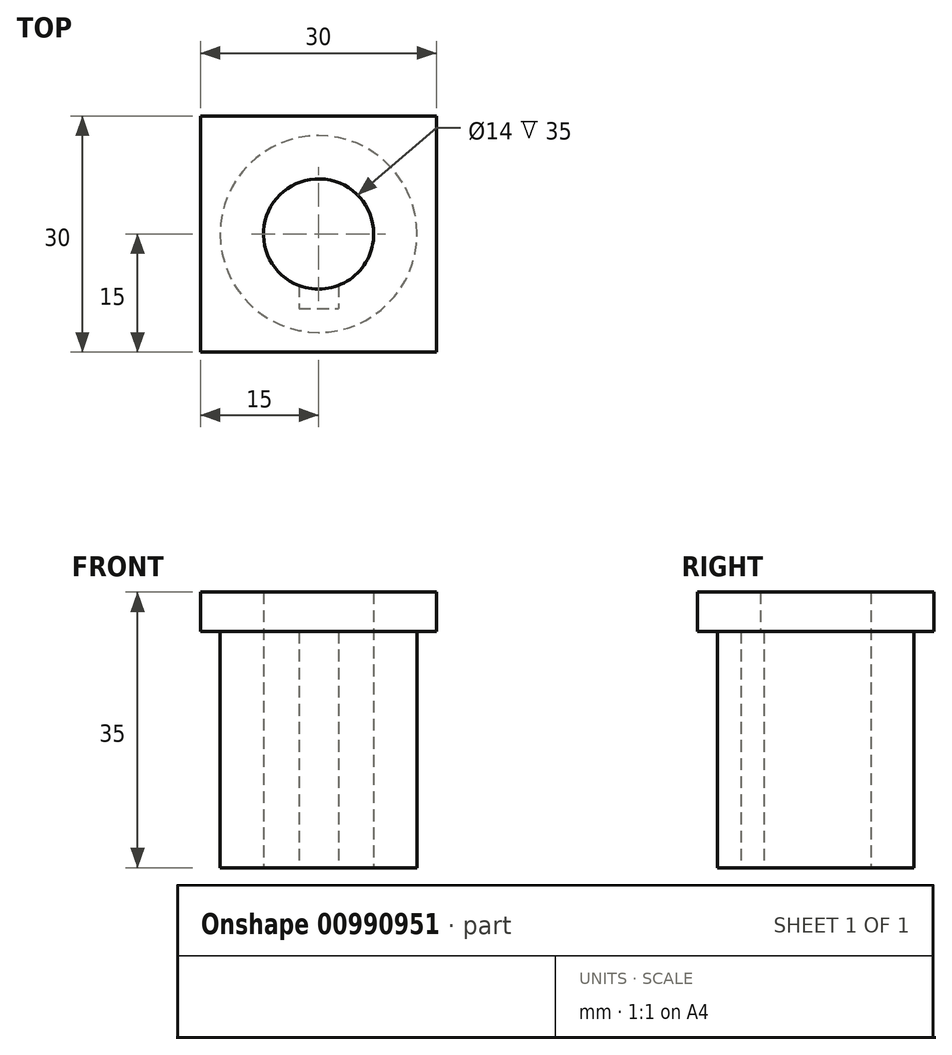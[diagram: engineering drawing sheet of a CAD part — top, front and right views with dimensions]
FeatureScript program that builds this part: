
annotation { "Feature Type Name" : "Feature", "Feature Type Description" : "" }
export const myFeature = defineFeature(function(context is Context, id is Id, definition is map)
    precondition{}
    {
        {
            var Q0;
            Q0=qCreatedBy(makeId("Top.planeOp"),FACE);
            var sketch = newSketch(context, id + "F0", { "sketchPlane" : qUnion([Q0])});
            skCircle(sketch, "E0", {"center": v(0, 0) * mm, "radius": 7 * mm});
            skLineSegment(sketch, "E1.bottom", {"start": v(15, -15) * mm, "end": v(-15, -15) * mm});
            skLineSegment(sketch, "E1.top", {"start": v(15, 15) * mm, "end": v(-15, 15) * mm});
            skLineSegment(sketch, "E1.left", {"start": v(15, -15) * mm, "end": v(15, 15) * mm});
            skLineSegment(sketch, "E1.right", {"start": v(-15, -15) * mm, "end": v(-15, 15) * mm});
            skLineSegment(sketch, "E2", {"start": v(0, 11.31) * mm, "end": v(0, -11.81) * mm, "construction": true});
            skLineSegment(sketch, "E3", {"start": v(-2.5, -6.54) * mm, "end": v(-2.5, -9.5) * mm});
            skLineSegment(sketch, "E4", {"start": v(-2.5, -9.5) * mm, "end": v(0, -9.5) * mm});
            skLineSegment(sketch, "E5.MirrorCS", {"start": v(2.5, -9.5) * mm, "end": v(0, -9.5) * mm});
            skLineSegment(sketch, "E6.MirrorCS", {"start": v(2.5, -6.54) * mm, "end": v(2.5, -9.5) * mm});
            skPoint(sketch, "E7", {"position": v(0, -7) * mm});
            skSolve(sketch);
        }
        {
            var Q0;
            Q0=makeQuery(id+"F0.imprint","IMPRINT",FACE,{"disambiguationData":[TD([[makeQuery(id+"F0.imprint","IMPRINT",EDGE,{"derivedFrom":sQuery(id+"F0.wireOp",EDGE,"E1.bottom")}),-1.0]])]});
            var Q1;
            {var subQ0=sQuery(id+"F0.wireOp",EDGE,"E0");var subQ2=makeQuery(id+"F0.imprint","IMPRINT",VERTEX,{"derivedFrom":subQ0});Q1=makeQuery(id+"F0.imprint","IMPRINT",FACE,{"disambiguationData":[TD([[makeQuery(id+"F0.imprint","IMPRINT",EDGE,{"disambiguationData":[TD([[subQ2,-1.0]])],"derivedFrom":subQ0}),1.0]])]});}
            var Q2;
            {var subQ0=sQuery(id+"F0.wireOp",EDGE,"E3");Q2=makeQuery(id+"F0.imprint","IMPRINT",FACE,{"disambiguationData":[TD([[makeQuery(id+"F0.imprint","IMPRINT",EDGE,{"derivedFrom":subQ0}),1.0]])]});}
            extrude(context, id + "F1", {"entities" : qUnion([Q0, Q1, Q2]), "depth" : 35 * mm, "offsetDistance" : 25 * mm});
        }
        {
            var Q0;
            {var subQ0=sQuery(id+"F0.wireOp",EDGE,"E0");var subQ2=makeQuery(id+"F0.imprint","IMPRINT",VERTEX,{"derivedFrom":subQ0});Q0=makeQuery(id+"F0.imprint","IMPRINT",FACE,{"disambiguationData":[TD([[makeQuery(id+"F0.imprint","IMPRINT",EDGE,{"disambiguationData":[TD([[subQ2,-1.0]])],"derivedFrom":subQ0}),1.0]])]});}
            var Q1;
            {var subQ0=sQuery(id+"F0.wireOp",EDGE,"E3");Q1=makeQuery(id+"F0.imprint","IMPRINT",FACE,{"disambiguationData":[TD([[makeQuery(id+"F0.imprint","IMPRINT",EDGE,{"derivedFrom":subQ0}),1.0]])]});}
            extrude(context, id + "F2", {"entities" : qUnion([Q0, Q1]), "operationType" : NewBodyOperationType.REMOVE, "depth" : 30 * mm, "offsetDistance" : 25 * mm});
        }
        {
            var Q0;
            Q0=makeQuery(id+"F1.opExtrude","CAP_FACE",FACE,{"disambiguationData":[OSD([sQuery(id+"F0.wireOp",EDGE,"E1.bottom"),sQuery(id+"F0.wireOp",EDGE,"E1.top"),sQuery(id+"F0.wireOp",EDGE,"E1.left"),sQuery(id+"F0.wireOp",EDGE,"E1.right")])],"isStart":false});
            var sketch = newSketch(context, id + "F3", { "sketchPlane" : qUnion([Q0])});
            skCircle(sketch, "E8", {"center": v(0, 0) * mm, "radius": 2.5 * mm});
            skSolve(sketch);
        }
        {
            var Q0;
            Q0=makeQuery(id+"F3.imprint","IMPRINT",FACE,{"disambiguationData":[TD([[makeQuery(id+"F3.imprint","IMPRINT",EDGE,{"derivedFrom":sQuery(id+"F3.wireOp",EDGE,"E8")}),1.0]])]});
            extrude(context, id + "F4", {"entities" : qUnion([Q0]), "operationType" : NewBodyOperationType.REMOVE, "endBound" : BoundingType.THROUGH_ALL, "oppositeDirection" : true, "depth" : 25 * mm, "offsetDistance" : 25 * mm});
        }
        {
            var Q0;
            Q0=makeQuery(id+"F0.imprint","IMPRINT",FACE,{"disambiguationData":[TD([[makeQuery(id+"F0.imprint","IMPRINT",EDGE,{"derivedFrom":sQuery(id+"F0.wireOp",EDGE,"E1.bottom")}),-1.0]])]});
            var sketch = newSketch(context, id + "F5", { "sketchPlane" : qUnion([Q0])});
            skCircle(sketch, "E9", {"center": v(0, 0) * mm, "radius": 12.5 * mm});
            skSolve(sketch);
        }
        {
            var Q0;
            Q0=makeQuery(id+"F5.imprint","IMPRINT",FACE,{"disambiguationData":[TD([[makeQuery(id+"F5.imprint","IMPRINT",EDGE,{"derivedFrom":sQuery(id+"F5.wireOp",EDGE,"E9")}),-1.0]])]});
            extrude(context, id + "F6", {"entities" : qUnion([Q0]), "operationType" : NewBodyOperationType.REMOVE, "depth" : 30 * mm, "offsetDistance" : 25 * mm});
        }
    });
